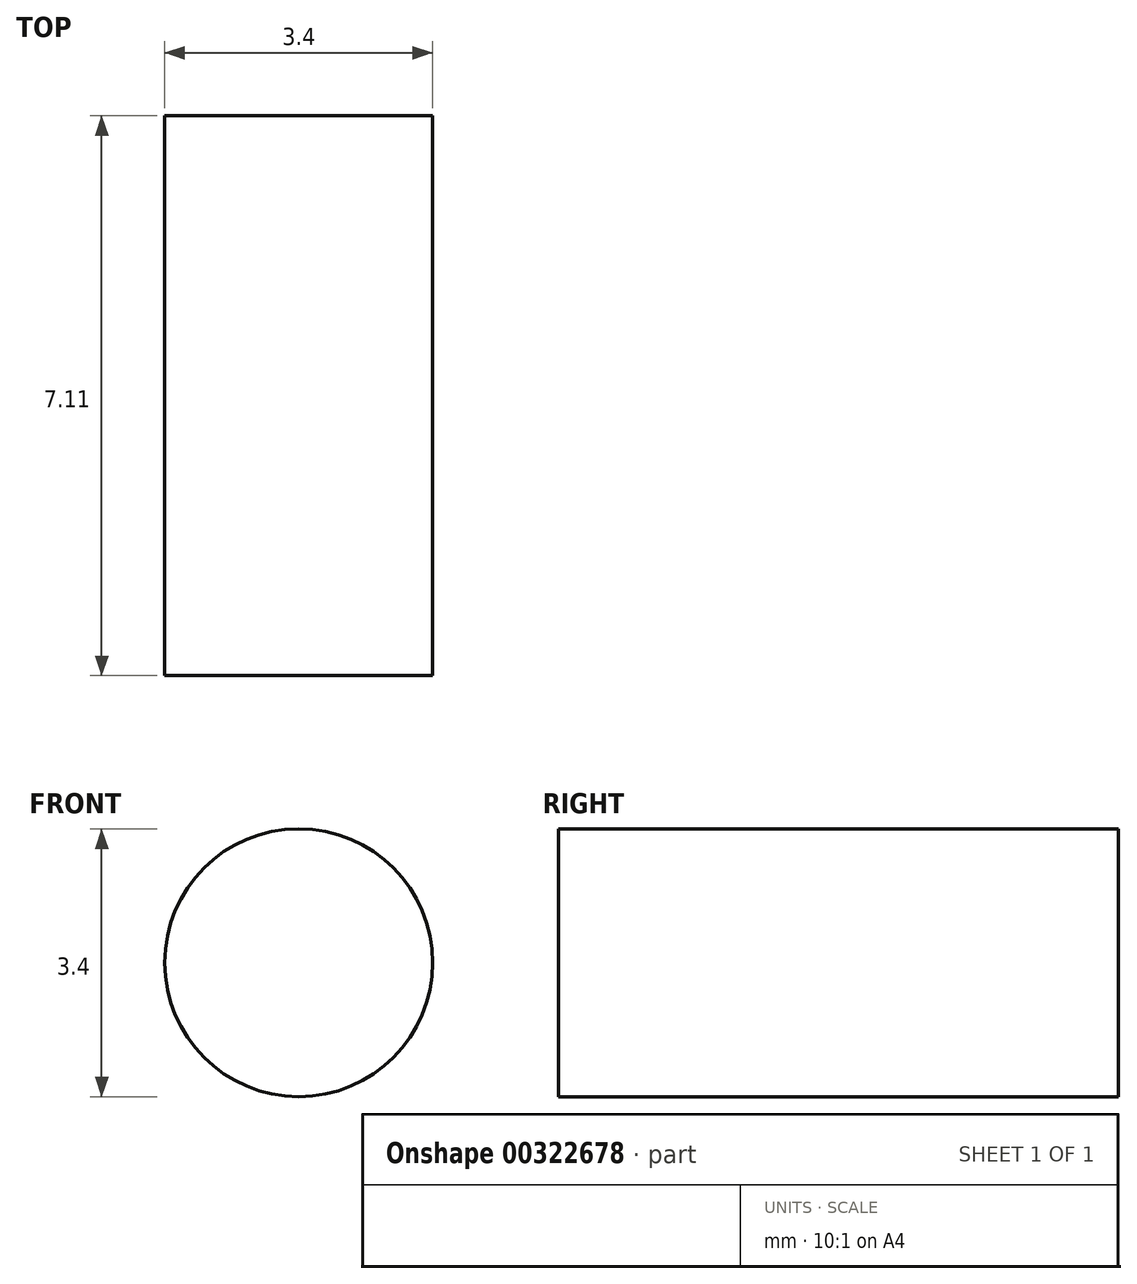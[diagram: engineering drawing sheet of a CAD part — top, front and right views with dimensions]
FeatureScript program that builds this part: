
annotation { "Feature Type Name" : "Feature", "Feature Type Description" : "" }
export const myFeature = defineFeature(function(context is Context, id is Id, definition is map)
    precondition{}
    {
        {
            var Q0;
            Q0=qCreatedBy(makeId("Front.planeOp"),FACE);
            var sketch = newSketch(context, id + "F0", { "sketchPlane" : qUnion([Q0])});
            skCircle(sketch, "E0", {"center": v(-19.53, 21.13) * mm, "radius": 1.7 * mm});
            skSolve(sketch);
        }
        {
            var Q0;
            Q0=makeQuery(id+"F0.imprint","IMPRINT",FACE,{"disambiguationData":[TD([[makeQuery(id+"F0.imprint","IMPRINT",EDGE,{"derivedFrom":sQuery(id+"F0.wireOp",EDGE,"E0")}),1.0]])]});
            extrude(context, id + "F1", {"entities" : qUnion([Q0]), "depth" : 7.11 * mm});
        }
    });
